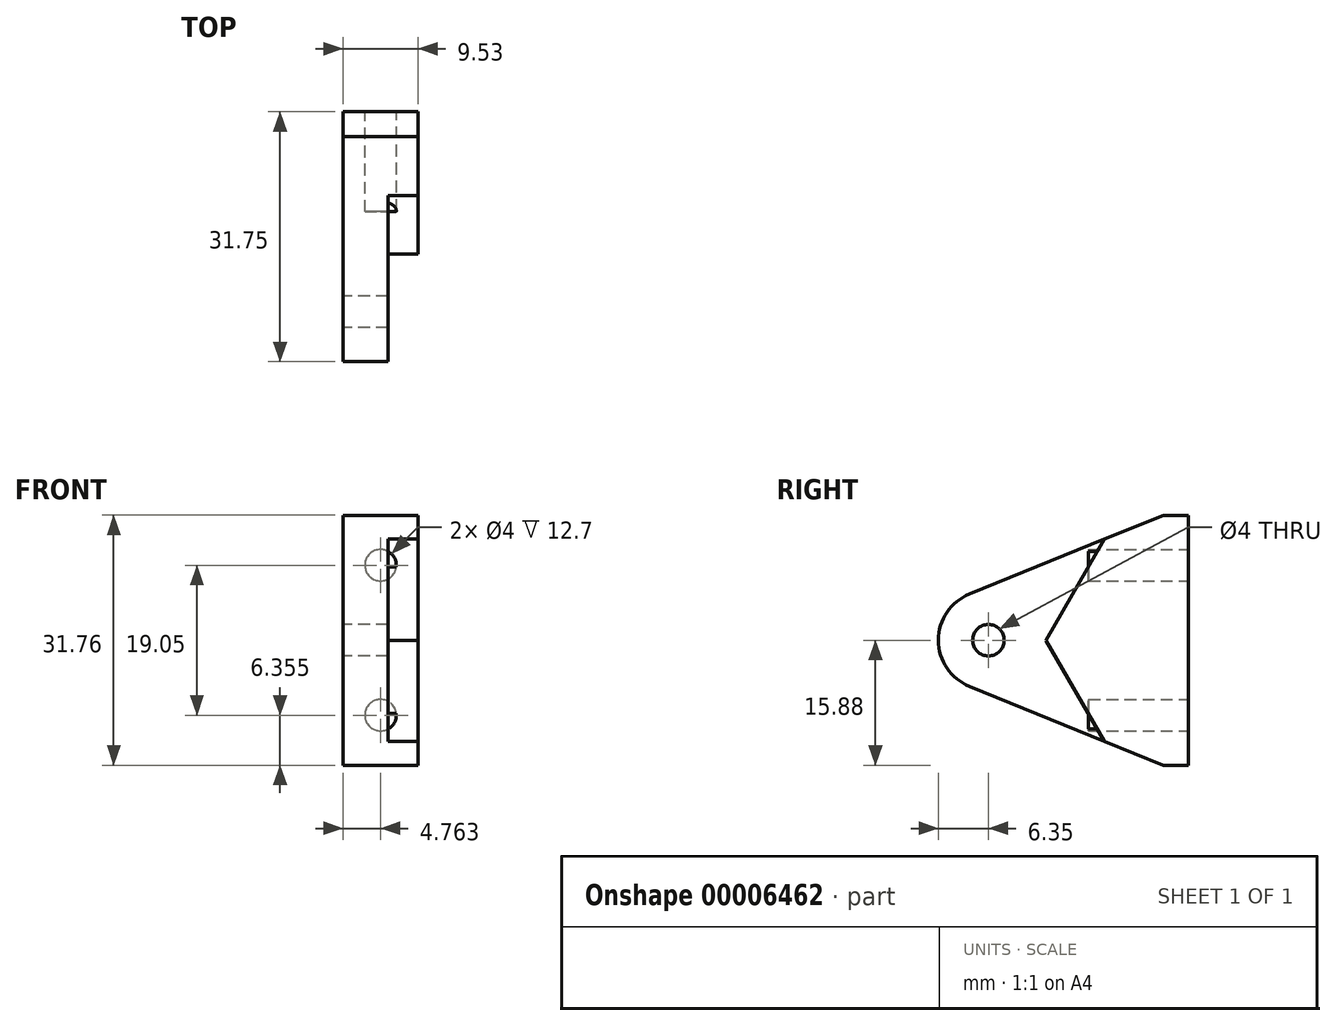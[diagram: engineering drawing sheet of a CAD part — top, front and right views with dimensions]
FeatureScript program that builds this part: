
annotation { "Feature Type Name" : "Feature", "Feature Type Description" : "" }
export const myFeature = defineFeature(function(context is Context, id is Id, definition is map)
    precondition{}
    {
        {
            var Q0;
            Q0=qCreatedBy(makeId("Right.planeOp"),FACE);
            var sketch = newSketch(context, id + "F0", { "sketchPlane" : qUnion([Q0])});
            skCircle(sketch, "E0", {"center": v(0, 0) * mm, "radius": 2 * mm});
            skArc(sketch, "E1", {"start": v(-2.39, 5.88) * mm, "mid": v(-6.35, 0) * mm, "end": v(-2.39, -5.88) * mm});
            skLineSegment(sketch, "E2", {"start": v(-2.39, 5.88) * mm, "end": v(22.23, 15.87) * mm});
            skLineSegment(sketch, "E3", {"start": v(22.23, -15.88) * mm, "end": v(-2.39, -5.88) * mm});
            skLineSegment(sketch, "E4", {"start": v(22.23, 15.87) * mm, "end": v(25.4, 15.87) * mm});
            skLineSegment(sketch, "E5", {"start": v(25.4, 15.87) * mm, "end": v(25.4, -15.87) * mm});
            skLineSegment(sketch, "E6", {"start": v(25.4, -15.88) * mm, "end": v(22.23, -15.88) * mm});
            skLineSegment(sketch, "E7.bottom", {"start": v(25.4, 11.53) * mm, "end": v(12.7, 11.53) * mm, "construction": true});
            skLineSegment(sketch, "E7.top", {"start": v(25.4, 7.53) * mm, "end": v(12.7, 7.53) * mm, "construction": true});
            skLineSegment(sketch, "E7.left", {"start": v(25.4, 11.53) * mm, "end": v(25.4, 7.52) * mm, "construction": true});
            skLineSegment(sketch, "E7.right", {"start": v(12.7, 11.53) * mm, "end": v(12.7, 7.52) * mm, "construction": true});
            skLineSegment(sketch, "E8.bottom", {"start": v(25.4, -11.53) * mm, "end": v(12.7, -11.52) * mm, "construction": true});
            skLineSegment(sketch, "E8.top", {"start": v(25.4, -7.53) * mm, "end": v(12.7, -7.52) * mm, "construction": true});
            skLineSegment(sketch, "E8.left", {"start": v(25.4, -11.53) * mm, "end": v(25.4, -7.52) * mm, "construction": true});
            skLineSegment(sketch, "E8.right", {"start": v(12.7, -11.53) * mm, "end": v(12.7, -7.52) * mm, "construction": true});
            skLineSegment(sketch, "E9", {"start": v(12.7, 11.53) * mm, "end": v(22.23, 15.87) * mm, "construction": true});
            skLineSegment(sketch, "E10", {"start": v(12.7, -11.53) * mm, "end": v(22.23, -15.87) * mm, "construction": true});
            skLineSegment(sketch, "E11", {"start": v(-6.35, 0) * mm, "end": v(25.4, 0) * mm, "construction": true});
            skSolve(sketch);
        }
        {
            var Q0;
            Q0 = qSketchRegion(id + "F0", true);
            extrude(context, id + "F1", {"entities" : qUnion([Q0]), "depth" : 9.52 * mm});
        }
        {
            var Q0;
            Q0=makeQuery(id+"F1.opExtrude","SWEPT_FACE",FACE,{"disambiguationData":[OSD([sQuery(id+"F0.wireOp",EDGE,"E5")])]});
            var sketch = newSketch(context, id + "F2", { "sketchPlane" : qUnion([Q0])});
            skCircle(sketch, "E12", {"center": v(-4.76, 9.52) * mm, "radius": 2 * mm});
            skCircle(sketch, "E13", {"center": v(-4.76, -9.53) * mm, "radius": 2 * mm});
            skLineSegment(sketch, "E14", {"start": v(-4.76, 9.52) * mm, "end": v(-4.76, -9.53) * mm, "construction": true});
            skLineSegment(sketch, "E15", {"start": v(-4.76, -9.53) * mm, "end": v(-4.76, -15.88) * mm, "construction": true});
            skLineSegment(sketch, "E16", {"start": v(-4.76, 9.52) * mm, "end": v(-4.76, 15.87) * mm, "construction": true});
            skSolve(sketch);
        }
        {
            var Q0;
            Q0 = qSketchRegion(id + "F2", true);
            extrude(context, id + "F3", {"entities" : qUnion([Q0]), "operationType" : NewBodyOperationType.REMOVE, "oppositeDirection" : true, "depth" : 12.7 * mm});
        }
        {
            var Q0;
            Q0=makeQuery(id+"F1.opExtrude","CAP_FACE",FACE,{"disambiguationData":[OSD([sQuery(id+"F0.wireOp",EDGE,"E0"),sQuery(id+"F0.wireOp",EDGE,"E1"),sQuery(id+"F0.wireOp",EDGE,"E2"),sQuery(id+"F0.wireOp",EDGE,"E3"),sQuery(id+"F0.wireOp",EDGE,"E4"),sQuery(id+"F0.wireOp",EDGE,"E5"),sQuery(id+"F0.wireOp",EDGE,"E6")])],"isStart":false});
            var sketch = newSketch(context, id + "F4", { "sketchPlane" : qUnion([Q0])});
            skLineSegment(sketch, "E17", {"start": v(7.33, 0) * mm, "end": v(14.74, -12.84) * mm});
            skLineSegment(sketch, "E18", {"start": v(7.33, 0) * mm, "end": v(14.74, 12.84) * mm});
            skLineSegment(sketch, "E19", {"start": v(14.74, 12.84) * mm, "end": v(-12.46, 7.05) * mm});
            skLineSegment(sketch, "E20", {"start": v(-12.46, 7.05) * mm, "end": v(-8.84, -9.97) * mm});
            skLineSegment(sketch, "E21", {"start": v(-8.84, -9.97) * mm, "end": v(14.74, -12.84) * mm});
            skPoint(sketch, "E22", {"position": v(0, 0) * mm});
            skSolve(sketch);
        }
        {
            var Q0;
            Q0 = qSketchRegion(id + "F4", true);
            extrude(context, id + "F5", {"entities" : qUnion([Q0]), "operationType" : NewBodyOperationType.REMOVE, "oppositeDirection" : true, "depth" : 3.8 * mm});
        }
    });
